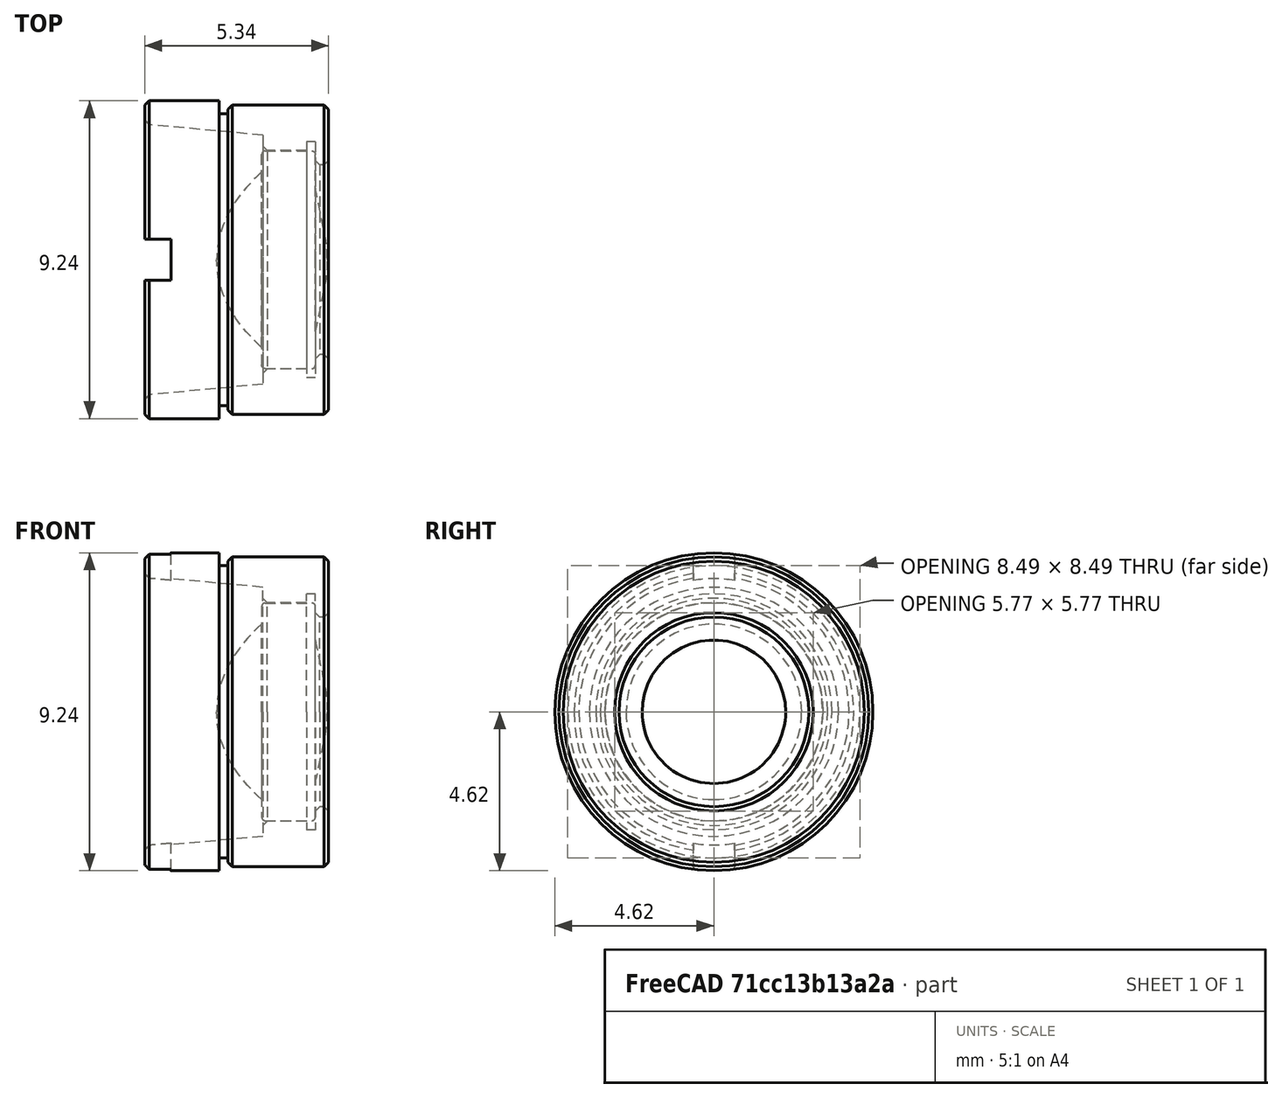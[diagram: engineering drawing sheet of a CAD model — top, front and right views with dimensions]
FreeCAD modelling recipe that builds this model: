
FCSTD DOCUMENT  (FreeCAD 1.1R44874 (Git))
Label: imported-stepfile-as-surface-source
License: All rights reserved
LicenseURL: https://en.wikipedia.org/wiki/All_rights_reserved
objects: App::Part×3, App::Point×3, Part::Feature×2, App::Link×2, App::LinkGroupPython×2, Part::FeaturePython×1
note: 3 computed .brp shape members not serialized (recipe doc carries the construction recipe); baked Part::Feature solids carry a one-line shape summary decoded from their .brp

FEATURE [Part::Feature] Part__Feature  label="TTN021329-E0W"
  shape: bbox 5.334 x 9.238 x 9.238 mm, 73 faces (baked)
FEATURE [Part::Feature] Part__Feature001  label="TTN021329-E0W001"
  shape: bbox 3.214 x 6.846 x 6.846 mm, 12 faces (baked)
FEATURE [App::Part] TTN021329_E0W  label="TTN021329-E0W002"
  Group = -> [Part__Feature,Part__Feature001]
  Origin = -> Origin
FEATURE [App::Point] Origin001
  Role = Origin
FEATURE [App::Point] Origin003
  Role = Origin
FEATURE [App::Link] Link  label="TTN021329-E0W003"
  LinkPlacement = pos=(10,0,0) rot=(1,0,1;0.401426rad)
  LinkedObject = -> Part__Feature001
  Placement = pos=(10,0,0) rot=(1,0,1;0.401426rad)
FEATURE [App::Point] Origin005  label="Origin006"
  Role = Origin
FEATURE [App::Link] Link001  label="TTN021329-E0W004"
  LinkedObject = -> Part__Feature
FEATURE [App::Part] Part  label="housing"
  Group = -> [Link001]
  Origin = -> Origin002
FEATURE [App::LinkGroupPython] OpticalLensGroup  # WARN: FeaturePython — macro-defined, semantics opaque (R4)
  AbsorptionLength = inf
  ElementList = -> [Link]
  GratingDiffractionOrder = 1
  GratingLinesOrientation = (0,0,1)
  GratingLinesPerMillimeter = 1000
  GratingType = 0
  LinkMode = 0
  ModifyPhiDomain = 0, 2*pi
  ModifyThetaDomain = -pi/2, pi/2
  OpticalType = 1
  Placement = pos=(0,9,0) rot=(0,1,0;-0.383972rad)
  PowerPhiDomain = 0, 2*pi
  PowerThetaDomain = -pi/2, pi/2
  RecordHits = false
  Reflectivity = 1
  RefractiveIndex = 2
FEATURE [App::Part] Part001  label="lens"
  Group = -> [OpticalLensGroup]
  Origin = -> Origin004
  Placement = pos=(-10,0,-20) rot=(8,0,1;0.541052rad)
FEATURE [App::LinkGroupPython] OpticalSurfaceSource  # WARN: FeaturePython — macro-defined, semantics opaque (R4)
  ActiveSurfaces = -> [Link]
  FanModeRayCount = 100
  LinkMode = 0
  MaxIntersectionsScale = 1
  MaxRayLengthScale = 1
  PhiDomain = 0, 2*pi
  PowerDensity = cos(theta)**2
  RadiusDomain = 0, 10
  RadiusResolutionNumericMode = 100000
  RandomNumberGeneratorMode = ?
  RaysPerIterationScale = 1
  RecordRays = false
  ThetaDomain = 0,pi/2
  ThetaResolutionNumericMode = 1000000
  UVSamplingInitialResolution = 5
  UVSamplingMaxRelAreaElementChange = 0.1
  Wavelength = 500
FEATURE [Part::FeaturePython] OpticalSimulationSettings  # WARN: FeaturePython — macro-defined, semantics opaque (R4)
  Active = true
  DistanceTolerance = 1e-06
  EnableStoreSingleShotData = true
  EndAfterHits = inf
  EndAfterIterations = inf
  EndAfterRays = 10000
  MaxIntersections = 100
  MaxRayLength = 1000
  RaysPerIteration = 100
  SequentialMode = false
  ShowRaysInContinuousMode = true
  StoreHitFanIndex = false
  StoreHitInitDirection = false
  StoreHitInitPhi = false
  StoreHitInitPoint = false
  StoreHitInitPower = false
  StoreHitInitTheta = false
  StoreHitInitWavelength = false
  StoreHitRayIndex = false
  StoreHitTotalFanCount = false
  StoreHitTotalRaysInFan = false
  WorkerProcessCount = num_cpus
